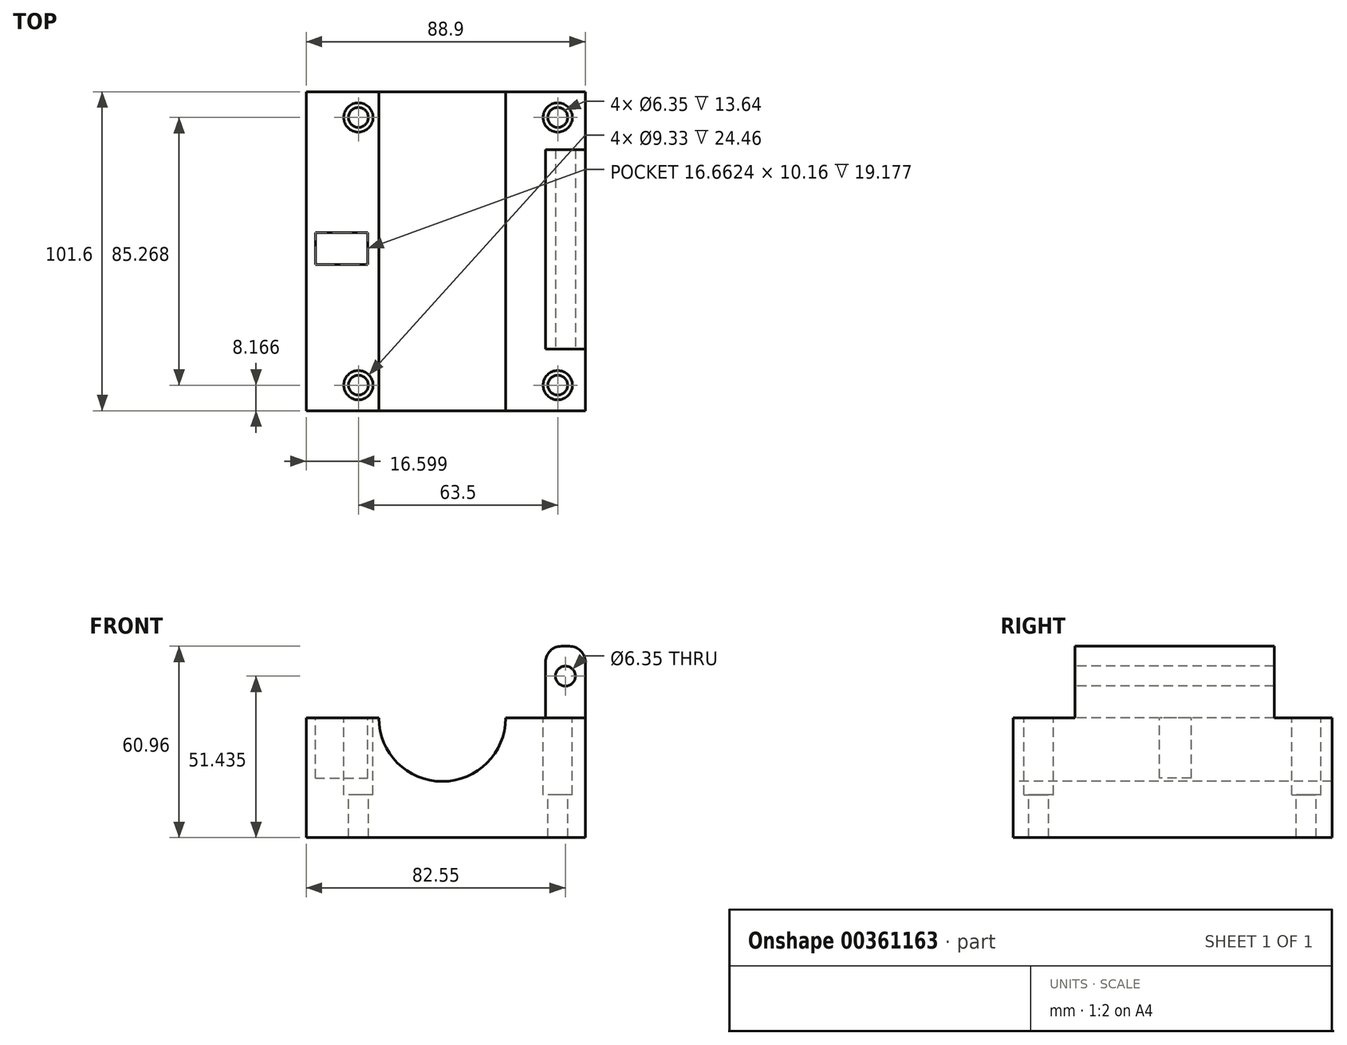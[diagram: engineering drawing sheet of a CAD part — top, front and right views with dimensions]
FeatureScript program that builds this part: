
annotation { "Feature Type Name" : "Feature", "Feature Type Description" : "" }
export const myFeature = defineFeature(function(context is Context, id is Id, definition is map)
    precondition{}
    {
        {
            var Q0;
            Q0=qCreatedBy(makeId("Front.planeOp"),FACE);
            var sketch = newSketch(context, id + "F0", { "sketchPlane" : qUnion([Q0])});
            skLineSegment(sketch, "E0.bottom", {"start": v(0, 0) * mm, "end": v(88.9, 0) * mm});
            skLineSegment(sketch, "E0.left", {"start": v(0, 0) * mm, "end": v(0, 38.1) * mm});
            skLineSegment(sketch, "E0.right", {"start": v(88.9, 0) * mm, "end": v(88.9, 38.1) * mm});
            skLineSegment(sketch, "E1", {"start": v(0, 38.1) * mm, "end": v(23.11, 38.1) * mm});
            skLineSegment(sketch, "E2", {"start": v(88.9, 38.1) * mm, "end": v(63.5, 38.1) * mm});
            skArc(sketch, "E3", {"start": v(23.11, 38.1) * mm, "mid": v(43.3, 17.9) * mm, "end": v(63.5, 38.1) * mm});
            skPoint(sketch, "E4.start.orphan", {"position": v(44.45, 0) * mm});
            skSolve(sketch);
        }
        {
            var Q0;
            Q0=makeQuery(id+"F0.imprint","IMPRINT",FACE,{"disambiguationData":[TD([[makeQuery(id+"F0.imprint","IMPRINT",EDGE,{"derivedFrom":sQuery(id+"F0.wireOp",EDGE,"E0.bottom")}),1.0]])]});
            extrude(context, id + "F1", {"entities" : qUnion([Q0]), "oppositeDirection" : true, "depth" : 101.6 * mm});
        }
        {
            var Q0;
            Q0=makeQuery(id+"F1.opExtrude","SWEPT_FACE",FACE,{"disambiguationData":[OSD([sQuery(id+"F0.wireOp",EDGE,"E1")])]});
            var sketch = newSketch(context, id + "F2", { "sketchPlane" : qUnion([Q0])});
            skCircle(sketch, "E5", {"center": v(16.6, 93.43) * mm, "radius": 4.74 * mm});
            skCircle(sketch, "E6", {"center": v(16.6, 8.17) * mm, "radius": 4.74 * mm});
            skCircle(sketch, "E7", {"center": v(80.1, 93.43) * mm, "radius": 4.74 * mm});
            skCircle(sketch, "E8", {"center": v(80.1, 8.17) * mm, "radius": 4.74 * mm});
            skSolve(sketch);
        }
        {
            var Q0;
            Q0=sQuery(id+"F2.wireOp",VERTEX,"E6.center");
            var Q1;
            Q1=sQuery(id+"F2.wireOp",VERTEX,"E5.center");
            var Q2;
            Q2=sQuery(id+"F2.wireOp",VERTEX,"E7.center");
            var Q3;
            Q3=sQuery(id+"F2.wireOp",VERTEX,"E8.center");
            var Q4;
            Q4=makeQuery(id+"F1.opExtrude","SWEPT_BODY",BODY,{"disambiguationData":[OSD([sQuery(id+"F0.wireOp",EDGE,"E0.bottom"),sQuery(id+"F0.wireOp",EDGE,"E0.left"),sQuery(id+"F0.wireOp",EDGE,"E0.right"),sQuery(id+"F0.wireOp",EDGE,"E1"),sQuery(id+"F0.wireOp",EDGE,"E2"),sQuery(id+"F0.wireOp",EDGE,"E3")])]});
            hole(context, id + "F3", {"style" : HoleStyle.C_BORE, "endStyle" : HoleEndStyle.THROUGH, "holeDiameter" : 6.35 * mm, "cBoreDiameter" : 9.33 * mm, "cBoreDepth" : 24.46 * mm, "isTappedThrough" : true, "tappedDepth" : 12.7 * mm, "tapClearance" : 3, "startFromSketch" : true, "locations" : qUnion([Q0, Q1, Q2, Q3]), "scope" : qUnion([Q4])});
        }
        {
            var Q0;
            Q0=makeQuery(id+"F1.opExtrude","SWEPT_FACE",FACE,{"disambiguationData":[OSD([sQuery(id+"F0.wireOp",EDGE,"E2")])]});
            var sketch = newSketch(context, id + "F4", { "sketchPlane" : qUnion([Q0])});
            skLineSegment(sketch, "E9.bottom", {"start": v(76.2, 83.19) * mm, "end": v(88.9, 83.19) * mm});
            skLineSegment(sketch, "E9.top", {"start": v(76.2, 19.69) * mm, "end": v(88.9, 19.69) * mm});
            skLineSegment(sketch, "E9.left", {"start": v(76.2, 83.19) * mm, "end": v(76.2, 19.69) * mm});
            skLineSegment(sketch, "E9.right", {"start": v(88.9, 83.19) * mm, "end": v(88.9, 19.69) * mm});
            skSolve(sketch);
        }
        {
            var Q0;
            Q0=makeQuery(id+"F4.imprint","IMPRINT",FACE,{"disambiguationData":[TD([[makeQuery(id+"F4.imprint","IMPRINT",EDGE,{"derivedFrom":sQuery(id+"F4.wireOp",EDGE,"E9.bottom")}),-1.0]])]});
            extrude(context, id + "F5", {"entities" : qUnion([Q0]), "operationType" : NewBodyOperationType.ADD, "depth" : 22.86 * mm});
        }
        {
            var Q0;
            Q0=makeQuery(id+"F5.opExtrude","SWEPT_FACE",FACE,{"disambiguationData":[OSD([sQuery(id+"F4.wireOp",EDGE,"E9.top")])]});
            var sketch = newSketch(context, id + "F6", { "sketchPlane" : qUnion([Q0])});
            skCircle(sketch, "E10", {"center": v(82.55, 51.44) * mm, "radius": 3.18 * mm});
            skPoint(sketch, "E10.centerSnap0", {"position": v(82.55, 60.96) * mm});
            skSolve(sketch);
        }
        {
            var Q0;
            Q0=sQuery(id+"F6.wireOp",VERTEX,"E10.center");
            var Q1;
            Q1=makeQuery(id+"F1.opExtrude","SWEPT_BODY",BODY,{"disambiguationData":[OSD([sQuery(id+"F0.wireOp",EDGE,"E0.bottom"),sQuery(id+"F0.wireOp",EDGE,"E0.left"),sQuery(id+"F0.wireOp",EDGE,"E0.right"),sQuery(id+"F0.wireOp",EDGE,"E1"),sQuery(id+"F0.wireOp",EDGE,"E2"),sQuery(id+"F0.wireOp",EDGE,"E3")])]});
            hole(context, id + "F7", {"style" : HoleStyle.SIMPLE, "endStyle" : HoleEndStyle.THROUGH, "holeDiameter" : 6.35 * mm, "isTappedThrough" : true, "tappedDepth" : 12.7 * mm, "tapClearance" : 3, "startFromSketch" : true, "locations" : qUnion([Q0]), "scope" : qUnion([Q1])});
        }
        {
            var Q0;
            Q0=makeQuery(id+"F5.opExtrude","CAP_EDGE",EDGE,{"disambiguationData":[OSD([sQuery(id+"F4.wireOp",EDGE,"E9.left")])],"isStart":false});
            var Q1;
            Q1=makeQuery(id+"F5.opExtrude","CAP_EDGE",EDGE,{"disambiguationData":[OSD([sQuery(id+"F4.wireOp",EDGE,"E9.right")])],"isStart":false});
            fillet(context, id + "F8", {"entities" : qUnion([Q0, Q1]), "radius" : 5.08 * mm, "tangentPropagation" : true, "allowEdgeOverflow" : false});
        }
        {
            var Q0;
            Q0=makeQuery(id+"F1.opExtrude","SWEPT_FACE",FACE,{"disambiguationData":[OSD([sQuery(id+"F0.wireOp",EDGE,"E1")])]});
            var sketch = newSketch(context, id + "F9", { "sketchPlane" : qUnion([Q0])});
            skLineSegment(sketch, "E11.bottom", {"start": v(2.92, 56.77) * mm, "end": v(19.58, 56.77) * mm});
            skLineSegment(sketch, "E11.top", {"start": v(2.92, 46.6) * mm, "end": v(19.58, 46.6) * mm});
            skLineSegment(sketch, "E11.left", {"start": v(2.92, 56.77) * mm, "end": v(2.92, 46.6) * mm});
            skLineSegment(sketch, "E11.right", {"start": v(19.58, 56.77) * mm, "end": v(19.58, 46.6) * mm});
            skSolve(sketch);
        }
        {
            var Q0;
            Q0=makeQuery(id+"F9.imprint","IMPRINT",FACE,{"disambiguationData":[TD([[makeQuery(id+"F9.imprint","IMPRINT",EDGE,{"derivedFrom":sQuery(id+"F9.wireOp",EDGE,"E11.bottom")}),-1.0]])]});
            extrude(context, id + "F10", {"entities" : qUnion([Q0]), "operationType" : NewBodyOperationType.REMOVE, "oppositeDirection" : true, "depth" : 19.18 * mm});
        }
    });
